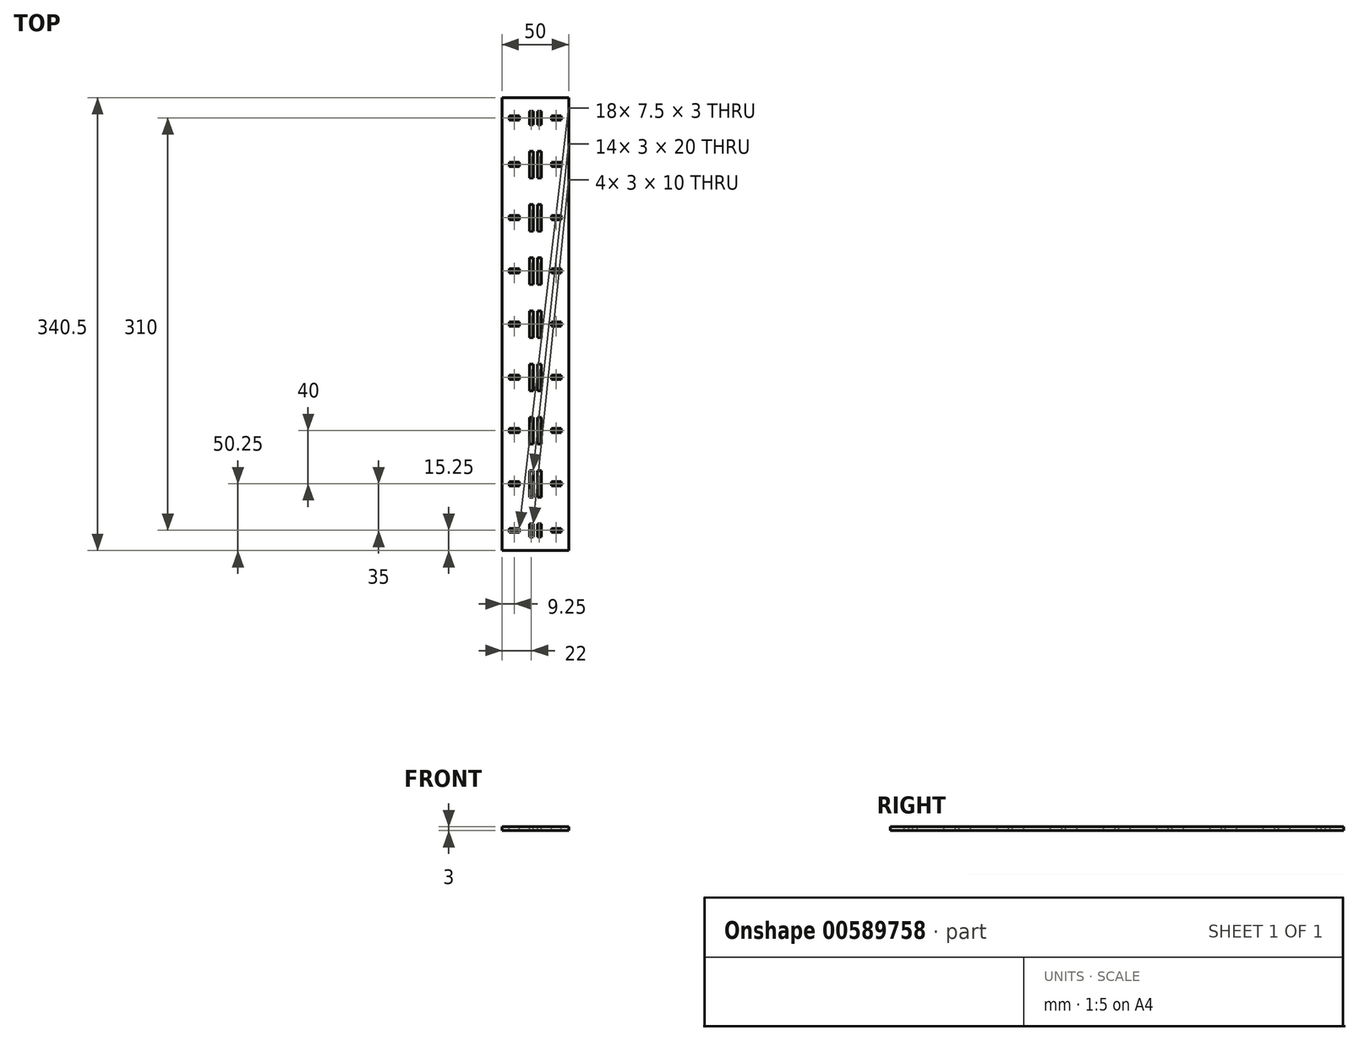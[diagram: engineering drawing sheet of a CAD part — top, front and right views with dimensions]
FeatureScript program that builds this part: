
annotation { "Feature Type Name" : "Feature", "Feature Type Description" : "" }
export const myFeature = defineFeature(function(context is Context, id is Id, definition is map)
    precondition{}
    {
        {
            var Q0;
            Q0=qCreatedBy(makeId("Top.planeOp"),FACE);
            var sketch = newSketch(context, id + "F0", { "sketchPlane" : qUnion([Q0])});
            skLineSegment(sketch, "E0.bottom", {"start": v(25, 140) * mm, "end": v(-25, 140) * mm});
            skLineSegment(sketch, "E0.top", {"start": v(25, -140) * mm, "end": v(-25, -140) * mm});
            skLineSegment(sketch, "E0.left", {"start": v(25, 140) * mm, "end": v(25, -140) * mm});
            skLineSegment(sketch, "E0.right", {"start": v(-25, 140) * mm, "end": v(-25, -140) * mm});
            skPoint(sketch, "E0.middle", {"position": v(0, 0) * mm});
            skSolve(sketch);
        }
        {
            var Q0;
            Q0=makeQuery(id+"F0.imprint","IMPRINT",FACE,{"disambiguationData":[TD([[makeQuery(id+"F0.imprint","IMPRINT",EDGE,{"derivedFrom":sQuery(id+"F0.wireOp",EDGE,"E0.bottom")}),1.0]])]});
            extrude(context, id + "F1", {"entities" : qUnion([Q0]), "depth" : 3 * mm, "offsetDistance" : 25 * mm});
        }
        {
            var Q0;
            Q0=makeQuery(id+"F1.opExtrude","CAP_FACE",FACE,{"disambiguationData":[OSD([sQuery(id+"F0.wireOp",EDGE,"E0.bottom"),sQuery(id+"F0.wireOp",EDGE,"E0.top"),sQuery(id+"F0.wireOp",EDGE,"E0.left"),sQuery(id+"F0.wireOp",EDGE,"E0.right")])],"isStart":false});
            var sketch = newSketch(context, id + "F2", { "sketchPlane" : qUnion([Q0])});
            skLineSegment(sketch, "E1", {"start": v(0, 140) * mm, "end": v(0, -140) * mm, "construction": true});
            skLineSegment(sketch, "E2.bottom", {"start": v(1.5, 140) * mm, "end": v(-1.5, 140) * mm, "construction": true});
            skLineSegment(sketch, "E2.top", {"start": v(1.5, -140) * mm, "end": v(-1.5, -140) * mm, "construction": true});
            skLineSegment(sketch, "E2.left", {"start": v(1.5, 140) * mm, "end": v(1.5, 130) * mm, "construction": true});
            skLineSegment(sketch, "E2.right", {"start": v(-1.5, 140) * mm, "end": v(-1.5, 130) * mm, "construction": true});
            skPoint(sketch, "E2.middle", {"position": v(0, 0) * mm});
            skLineSegment(sketch, "E3.bottom", {"start": v(1.5, 130) * mm, "end": v(4.5, 130) * mm});
            skLineSegment(sketch, "E3.top", {"start": v(1.5, 110) * mm, "end": v(4.5, 110) * mm});
            skLineSegment(sketch, "E3.right", {"start": v(4.5, 130) * mm, "end": v(4.5, 110) * mm});
            skLineSegment(sketch, "E4.trimOffspring", {"start": v(1.5, 110) * mm, "end": v(1.5, -140) * mm, "construction": true});
            skLineSegment(sketch, "E5", {"start": v(1.5, 130) * mm, "end": v(1.5, 110) * mm});
            skLineSegment(sketch, "E6.0.1.0", {"start": v(4.5, 90) * mm, "end": v(4.5, 70) * mm});
            skLineSegment(sketch, "E6.0.1.1", {"start": v(1.5, 90) * mm, "end": v(4.5, 90) * mm});
            skLineSegment(sketch, "E6.0.1.2", {"start": v(1.5, 90) * mm, "end": v(1.5, 70) * mm});
            skLineSegment(sketch, "E6.0.1.3", {"start": v(1.5, 70) * mm, "end": v(4.5, 70) * mm});
            skLineSegment(sketch, "E6.0.2.0", {"start": v(4.5, 50) * mm, "end": v(4.5, 30) * mm});
            skLineSegment(sketch, "E6.0.2.1", {"start": v(1.5, 50) * mm, "end": v(4.5, 50) * mm});
            skLineSegment(sketch, "E6.0.2.2", {"start": v(1.5, 50) * mm, "end": v(1.5, 30) * mm});
            skLineSegment(sketch, "E6.0.2.3", {"start": v(1.5, 30) * mm, "end": v(4.5, 30) * mm});
            skLineSegment(sketch, "E6.0.3.0", {"start": v(4.5, 10) * mm, "end": v(4.5, -10) * mm});
            skLineSegment(sketch, "E6.0.3.1", {"start": v(1.5, 10) * mm, "end": v(4.5, 10) * mm});
            skLineSegment(sketch, "E6.0.3.2", {"start": v(1.5, 10) * mm, "end": v(1.5, -10) * mm});
            skLineSegment(sketch, "E6.0.3.3", {"start": v(1.5, -10) * mm, "end": v(4.5, -10) * mm});
            skLineSegment(sketch, "E6.0.4.0", {"start": v(4.5, -30) * mm, "end": v(4.5, -50) * mm});
            skLineSegment(sketch, "E6.0.4.1", {"start": v(1.5, -30) * mm, "end": v(4.5, -30) * mm});
            skLineSegment(sketch, "E6.0.4.2", {"start": v(1.5, -30) * mm, "end": v(1.5, -50) * mm});
            skLineSegment(sketch, "E6.0.4.3", {"start": v(1.5, -50) * mm, "end": v(4.5, -50) * mm});
            skLineSegment(sketch, "E6.0.5.0", {"start": v(4.5, -70) * mm, "end": v(4.5, -90) * mm});
            skLineSegment(sketch, "E6.0.5.1", {"start": v(1.5, -70) * mm, "end": v(4.5, -70) * mm});
            skLineSegment(sketch, "E6.0.5.2", {"start": v(1.5, -70) * mm, "end": v(1.5, -90) * mm});
            skLineSegment(sketch, "E6.0.5.3", {"start": v(1.5, -90) * mm, "end": v(4.5, -90) * mm});
            skLineSegment(sketch, "E6.0.6.0", {"start": v(4.5, -110) * mm, "end": v(4.5, -130) * mm});
            skLineSegment(sketch, "E6.0.6.1", {"start": v(1.5, -110) * mm, "end": v(4.5, -110) * mm});
            skLineSegment(sketch, "E6.0.6.2", {"start": v(1.5, -110) * mm, "end": v(1.5, -130) * mm});
            skLineSegment(sketch, "E6.0.6.3", {"start": v(1.5, -130) * mm, "end": v(4.5, -130) * mm});
            skLineSegment(sketch, "E6.direction1", {"start": v(4.5, 110) * mm, "end": v(29.5, 110) * mm, "construction": true});
            skLineSegment(sketch, "E6.direction2", {"start": v(4.5, 110) * mm, "end": v(4.5, 70) * mm, "construction": true});
            skLineSegment(sketch, "E7.bottom", {"start": v(-1.5, 130) * mm, "end": v(-4.5, 130) * mm});
            skLineSegment(sketch, "E7.top", {"start": v(-1.5, 110) * mm, "end": v(-4.5, 110) * mm});
            skLineSegment(sketch, "E7.right", {"start": v(-4.5, 130) * mm, "end": v(-4.5, 110) * mm});
            skLineSegment(sketch, "E8.trimOffspring", {"start": v(-1.5, 110) * mm, "end": v(-1.5, -140) * mm, "construction": true});
            skLineSegment(sketch, "E9", {"start": v(-1.5, 130) * mm, "end": v(-1.5, 110) * mm});
            skLineSegment(sketch, "E10.0.1.0", {"start": v(-1.5, 90) * mm, "end": v(-4.5, 90) * mm});
            skLineSegment(sketch, "E10.0.1.1", {"start": v(-1.5, 90) * mm, "end": v(-1.5, 70) * mm});
            skLineSegment(sketch, "E10.0.1.2", {"start": v(-4.5, 90) * mm, "end": v(-4.5, 70) * mm});
            skLineSegment(sketch, "E10.0.1.3", {"start": v(-1.5, 70) * mm, "end": v(-4.5, 70) * mm});
            skLineSegment(sketch, "E10.0.2.0", {"start": v(-1.5, 50) * mm, "end": v(-4.5, 50) * mm});
            skLineSegment(sketch, "E10.0.2.1", {"start": v(-1.5, 50) * mm, "end": v(-1.5, 30) * mm});
            skLineSegment(sketch, "E10.0.2.2", {"start": v(-4.5, 50) * mm, "end": v(-4.5, 30) * mm});
            skLineSegment(sketch, "E10.0.2.3", {"start": v(-1.5, 30) * mm, "end": v(-4.5, 30) * mm});
            skLineSegment(sketch, "E10.0.3.0", {"start": v(-1.5, 10) * mm, "end": v(-4.5, 10) * mm});
            skLineSegment(sketch, "E10.0.3.1", {"start": v(-1.5, 10) * mm, "end": v(-1.5, -10) * mm});
            skLineSegment(sketch, "E10.0.3.2", {"start": v(-4.5, 10) * mm, "end": v(-4.5, -10) * mm});
            skLineSegment(sketch, "E10.0.3.3", {"start": v(-1.5, -10) * mm, "end": v(-4.5, -10) * mm});
            skLineSegment(sketch, "E10.0.4.0", {"start": v(-1.5, -30) * mm, "end": v(-4.5, -30) * mm});
            skLineSegment(sketch, "E10.0.4.1", {"start": v(-1.5, -30) * mm, "end": v(-1.5, -50) * mm});
            skLineSegment(sketch, "E10.0.4.2", {"start": v(-4.5, -30) * mm, "end": v(-4.5, -50) * mm});
            skLineSegment(sketch, "E10.0.4.3", {"start": v(-1.5, -50) * mm, "end": v(-4.5, -50) * mm});
            skLineSegment(sketch, "E10.0.5.0", {"start": v(-1.5, -70) * mm, "end": v(-4.5, -70) * mm});
            skLineSegment(sketch, "E10.0.5.1", {"start": v(-1.5, -70) * mm, "end": v(-1.5, -90) * mm});
            skLineSegment(sketch, "E10.0.5.2", {"start": v(-4.5, -70) * mm, "end": v(-4.5, -90) * mm});
            skLineSegment(sketch, "E10.0.5.3", {"start": v(-1.5, -90) * mm, "end": v(-4.5, -90) * mm});
            skLineSegment(sketch, "E10.0.6.0", {"start": v(-1.5, -110) * mm, "end": v(-4.5, -110) * mm});
            skLineSegment(sketch, "E10.0.6.1", {"start": v(-1.5, -110) * mm, "end": v(-1.5, -130) * mm});
            skLineSegment(sketch, "E10.0.6.2", {"start": v(-4.5, -110) * mm, "end": v(-4.5, -130) * mm});
            skLineSegment(sketch, "E10.0.6.3", {"start": v(-1.5, -130) * mm, "end": v(-4.5, -130) * mm});
            skLineSegment(sketch, "E10.direction1", {"start": v(-4.5, 130) * mm, "end": v(20.5, 130) * mm, "construction": true});
            skLineSegment(sketch, "E10.direction2", {"start": v(-4.5, 130) * mm, "end": v(-4.5, 90) * mm, "construction": true});
            skSolve(sketch);
        }
        {
            var Q0;
            Q0=qSketchRegion(id+"F2",true);
            extrude(context, id + "F3", {"entities" : qUnion([Q0]), "operationType" : NewBodyOperationType.REMOVE, "oppositeDirection" : true, "depth" : 25 * mm, "offsetDistance" : 25 * mm});
        }
        {
            var Q0;
            Q0=makeQuery(id+"F1.opExtrude","CAP_FACE",FACE,{"disambiguationData":[OSD([sQuery(id+"F0.wireOp",EDGE,"E0.bottom"),sQuery(id+"F0.wireOp",EDGE,"E0.top"),sQuery(id+"F0.wireOp",EDGE,"E0.left"),sQuery(id+"F0.wireOp",EDGE,"E0.right")])],"isStart":false});
            var sketch = newSketch(context, id + "F4", { "sketchPlane" : qUnion([Q0])});
            skLineSegment(sketch, "E11", {"start": v(4.5, 120) * mm, "end": v(12, 120) * mm, "construction": true});
            skLineSegment(sketch, "E12", {"start": v(12, 120) * mm, "end": v(19.5, 120) * mm, "construction": true});
            skLineSegment(sketch, "E13.bottom", {"start": v(19.5, 121.5) * mm, "end": v(12, 121.5) * mm});
            skLineSegment(sketch, "E13.top", {"start": v(19.5, 118.5) * mm, "end": v(12, 118.5) * mm});
            skLineSegment(sketch, "E13.left", {"start": v(19.5, 121.5) * mm, "end": v(19.5, 118.5) * mm});
            skLineSegment(sketch, "E13.right", {"start": v(12, 121.5) * mm, "end": v(12, 118.5) * mm});
            skPoint(sketch, "E13.middle", {"position": v(15.75, 120) * mm});
            skLineSegment(sketch, "E14.0.1.0", {"start": v(19.5, 81.5) * mm, "end": v(12, 81.5) * mm});
            skLineSegment(sketch, "E14.0.1.1", {"start": v(12, 81.5) * mm, "end": v(12, 78.5) * mm});
            skLineSegment(sketch, "E14.0.1.2", {"start": v(19.5, 78.5) * mm, "end": v(12, 78.5) * mm});
            skLineSegment(sketch, "E14.0.1.3", {"start": v(19.5, 81.5) * mm, "end": v(19.5, 78.5) * mm});
            skLineSegment(sketch, "E14.0.2.0", {"start": v(19.5, 41.5) * mm, "end": v(12, 41.5) * mm});
            skLineSegment(sketch, "E14.0.2.1", {"start": v(12, 41.5) * mm, "end": v(12, 38.5) * mm});
            skLineSegment(sketch, "E14.0.2.2", {"start": v(19.5, 38.5) * mm, "end": v(12, 38.5) * mm});
            skLineSegment(sketch, "E14.0.2.3", {"start": v(19.5, 41.5) * mm, "end": v(19.5, 38.5) * mm});
            skLineSegment(sketch, "E14.0.3.0", {"start": v(19.5, 1.5) * mm, "end": v(12, 1.5) * mm});
            skLineSegment(sketch, "E14.0.3.1", {"start": v(12, 1.5) * mm, "end": v(12, -1.5) * mm});
            skLineSegment(sketch, "E14.0.3.2", {"start": v(19.5, -1.5) * mm, "end": v(12, -1.5) * mm});
            skLineSegment(sketch, "E14.0.3.3", {"start": v(19.5, 1.5) * mm, "end": v(19.5, -1.5) * mm});
            skLineSegment(sketch, "E14.0.4.0", {"start": v(19.5, -38.5) * mm, "end": v(12, -38.5) * mm});
            skLineSegment(sketch, "E14.0.4.1", {"start": v(12, -38.5) * mm, "end": v(12, -41.5) * mm});
            skLineSegment(sketch, "E14.0.4.2", {"start": v(19.5, -41.5) * mm, "end": v(12, -41.5) * mm});
            skLineSegment(sketch, "E14.0.4.3", {"start": v(19.5, -38.5) * mm, "end": v(19.5, -41.5) * mm});
            skLineSegment(sketch, "E14.0.5.0", {"start": v(19.5, -78.5) * mm, "end": v(12, -78.5) * mm});
            skLineSegment(sketch, "E14.0.5.1", {"start": v(12, -78.5) * mm, "end": v(12, -81.5) * mm});
            skLineSegment(sketch, "E14.0.5.2", {"start": v(19.5, -81.5) * mm, "end": v(12, -81.5) * mm});
            skLineSegment(sketch, "E14.0.5.3", {"start": v(19.5, -78.5) * mm, "end": v(19.5, -81.5) * mm});
            skLineSegment(sketch, "E14.0.6.0", {"start": v(19.5, -118.5) * mm, "end": v(12, -118.5) * mm});
            skLineSegment(sketch, "E14.0.6.1", {"start": v(12, -118.5) * mm, "end": v(12, -121.5) * mm});
            skLineSegment(sketch, "E14.0.6.2", {"start": v(19.5, -121.5) * mm, "end": v(12, -121.5) * mm});
            skLineSegment(sketch, "E14.0.6.3", {"start": v(19.5, -118.5) * mm, "end": v(19.5, -121.5) * mm});
            skLineSegment(sketch, "E14.direction1", {"start": v(12, 118.5) * mm, "end": v(37, 118.5) * mm, "construction": true});
            skLineSegment(sketch, "E14.direction2", {"start": v(12, 118.5) * mm, "end": v(12, 78.5) * mm, "construction": true});
            skLineSegment(sketch, "E15", {"start": v(0, 140) * mm, "end": v(0, 132.73) * mm, "construction": true});
            skPoint(sketch, "E15.endSnap0", {"position": v(0, 140) * mm});
            skLineSegment(sketch, "E16.MirrorCS", {"start": v(-19.5, 121.5) * mm, "end": v(-12, 121.5) * mm});
            skLineSegment(sketch, "E17.MirrorCS", {"start": v(-19.5, 118.5) * mm, "end": v(-12, 118.5) * mm});
            skLineSegment(sketch, "E18.MirrorCS", {"start": v(-12, 121.5) * mm, "end": v(-12, 118.5) * mm});
            skLineSegment(sketch, "E19.MirrorCS", {"start": v(-12, 120) * mm, "end": v(-19.5, 120) * mm, "construction": true});
            skLineSegment(sketch, "E20.MirrorCS", {"start": v(-19.5, 121.5) * mm, "end": v(-19.5, 118.5) * mm});
            skLineSegment(sketch, "E21.MirrorCS", {"start": v(-19.5, -78.5) * mm, "end": v(-19.5, -81.5) * mm});
            skLineSegment(sketch, "E22.MirrorCS", {"start": v(-19.5, 41.5) * mm, "end": v(-19.5, 38.5) * mm});
            skLineSegment(sketch, "E23.MirrorCS", {"start": v(-19.5, 81.5) * mm, "end": v(-12, 81.5) * mm});
            skLineSegment(sketch, "E24.MirrorCS", {"start": v(-12, 81.5) * mm, "end": v(-12, 78.5) * mm});
            skLineSegment(sketch, "E25.MirrorCS", {"start": v(-19.5, 78.5) * mm, "end": v(-12, 78.5) * mm});
            skLineSegment(sketch, "E26.MirrorCS", {"start": v(-19.5, -78.5) * mm, "end": v(-12, -78.5) * mm});
            skLineSegment(sketch, "E27.MirrorCS", {"start": v(-19.5, -38.5) * mm, "end": v(-12, -38.5) * mm});
            skLineSegment(sketch, "E28.MirrorCS", {"start": v(-19.5, -118.5) * mm, "end": v(-12, -118.5) * mm});
            skLineSegment(sketch, "E29.MirrorCS", {"start": v(-12, -38.5) * mm, "end": v(-12, -41.5) * mm});
            skLineSegment(sketch, "E30.MirrorCS", {"start": v(-19.5, -1.5) * mm, "end": v(-12, -1.5) * mm});
            skLineSegment(sketch, "E31.MirrorCS", {"start": v(-12, -118.5) * mm, "end": v(-12, -121.5) * mm});
            skLineSegment(sketch, "E32.MirrorCS", {"start": v(-19.5, -118.5) * mm, "end": v(-19.5, -121.5) * mm});
            skLineSegment(sketch, "E33.MirrorCS", {"start": v(-19.5, -41.5) * mm, "end": v(-12, -41.5) * mm});
            skLineSegment(sketch, "E34.MirrorCS", {"start": v(-19.5, 1.5) * mm, "end": v(-12, 1.5) * mm});
            skLineSegment(sketch, "E35.MirrorCS", {"start": v(-12, 1.5) * mm, "end": v(-12, -1.5) * mm});
            skLineSegment(sketch, "E36.MirrorCS", {"start": v(-12, -78.5) * mm, "end": v(-12, -81.5) * mm});
            skLineSegment(sketch, "E37.MirrorCS", {"start": v(-19.5, 81.5) * mm, "end": v(-19.5, 78.5) * mm});
            skLineSegment(sketch, "E38.MirrorCS", {"start": v(-19.5, 41.5) * mm, "end": v(-12, 41.5) * mm});
            skLineSegment(sketch, "E39.MirrorCS", {"start": v(-19.5, -121.5) * mm, "end": v(-12, -121.5) * mm});
            skLineSegment(sketch, "E40.MirrorCS", {"start": v(-12, 41.5) * mm, "end": v(-12, 38.5) * mm});
            skLineSegment(sketch, "E41.MirrorCS", {"start": v(-19.5, 38.5) * mm, "end": v(-12, 38.5) * mm});
            skLineSegment(sketch, "E42.MirrorCS", {"start": v(-19.5, -81.5) * mm, "end": v(-12, -81.5) * mm});
            skLineSegment(sketch, "E43.MirrorCS", {"start": v(-19.5, 1.5) * mm, "end": v(-19.5, -1.5) * mm});
            skLineSegment(sketch, "E44.MirrorCS", {"start": v(-19.5, -38.5) * mm, "end": v(-19.5, -41.5) * mm});
            skPoint(sketch, "E45.MirrorP", {"position": v(-15.75, 120) * mm});
            skLineSegment(sketch, "E46.MirrorCS", {"start": v(-12, 118.5) * mm, "end": v(-12, 78.5) * mm, "construction": true});
            skLineSegment(sketch, "E47.MirrorCS", {"start": v(-12, 118.5) * mm, "end": v(-37, 118.5) * mm, "construction": true});
            skSolve(sketch);
        }
        {
            var Q0;
            Q0=qSketchRegion(id+"F4",true);
            extrude(context, id + "F5", {"entities" : qUnion([Q0]), "operationType" : NewBodyOperationType.REMOVE, "oppositeDirection" : true, "depth" : 25 * mm, "offsetDistance" : 25 * mm});
        }
        {
            var Q0;
            Q0=makeQuery(id+"F1.opExtrude","CAP_FACE",FACE,{"disambiguationData":[OSD([sQuery(id+"F0.wireOp",EDGE,"E0.bottom"),sQuery(id+"F0.wireOp",EDGE,"E0.top"),sQuery(id+"F0.wireOp",EDGE,"E0.left"),sQuery(id+"F0.wireOp",EDGE,"E0.right")])],"isStart":false});
            var sketch = newSketch(context, id + "F6", { "sketchPlane" : qUnion([Q0])});
            skLineSegment(sketch, "E48.bottom", {"start": v(-25, 140) * mm, "end": v(25, 140) * mm});
            skLineSegment(sketch, "E48.top", {"start": v(-25, 170.25) * mm, "end": v(25, 170.25) * mm});
            skLineSegment(sketch, "E48.left", {"start": v(-25, 140) * mm, "end": v(-25, 170.25) * mm});
            skLineSegment(sketch, "E48.right", {"start": v(25, 140) * mm, "end": v(25, 170.25) * mm});
            skLineSegment(sketch, "E49.MirrorCS", {"start": v(-25, -140) * mm, "end": v(-25, -170.25) * mm});
            skLineSegment(sketch, "E50.MirrorCS", {"start": v(-25, -170.25) * mm, "end": v(25, -170.25) * mm});
            skLineSegment(sketch, "E51.MirrorCS", {"start": v(-25, -140) * mm, "end": v(25, -140) * mm});
            skLineSegment(sketch, "E52.MirrorCS", {"start": v(25, -140) * mm, "end": v(25, -170.25) * mm});
            skSolve(sketch);
        }
        {
            var Q0;
            Q0 = qSketchRegion(id + "F6", true);
            extrude(context, id + "F7", {"entities" : qUnion([Q0]), "operationType" : NewBodyOperationType.ADD, "oppositeDirection" : true, "depth" : 3 * mm, "offsetDistance" : 25 * mm});
        }
        {
            var Q0;
            Q0=makeQuery(id+"F7.boolean.opBoolean","MERGE",FACE,{"derivedFrom":[makeQuery(id+"F1.opExtrude","CAP_FACE",FACE,{"disambiguationData":[OSD([sQuery(id+"F0.wireOp",EDGE,"E0.bottom"),sQuery(id+"F0.wireOp",EDGE,"E0.top"),sQuery(id+"F0.wireOp",EDGE,"E0.left"),sQuery(id+"F0.wireOp",EDGE,"E0.right")])],"isStart":false}),makeQuery(id+"F7.opExtrude","CAP_FACE",FACE,{"disambiguationData":[OSD([sQuery(id+"F6.wireOp",EDGE,"E48.bottom"),sQuery(id+"F6.wireOp",EDGE,"E48.top"),sQuery(id+"F6.wireOp",EDGE,"E48.left"),sQuery(id+"F6.wireOp",EDGE,"E48.right")])],"isStart":true}),makeQuery(id+"F7.opExtrude","CAP_FACE",FACE,{"disambiguationData":[OSD([sQuery(id+"F6.wireOp",EDGE,"E49.MirrorCS"),sQuery(id+"F6.wireOp",EDGE,"E50.MirrorCS"),sQuery(id+"F6.wireOp",EDGE,"E51.MirrorCS"),sQuery(id+"F6.wireOp",EDGE,"E52.MirrorCS")])],"isStart":true})]});
            var sketch = newSketch(context, id + "F8", { "sketchPlane" : qUnion([Q0])});
            skLineSegment(sketch, "E53", {"start": v(-1.5, 130) * mm, "end": v(-1.5, 150) * mm, "construction": true});
            skLineSegment(sketch, "E54.bottom", {"start": v(-1.5, 150) * mm, "end": v(-4.5, 150) * mm});
            skLineSegment(sketch, "E54.top", {"start": v(-1.5, 160) * mm, "end": v(-4.5, 160) * mm});
            skLineSegment(sketch, "E54.left", {"start": v(-1.5, 150) * mm, "end": v(-1.5, 160) * mm});
            skLineSegment(sketch, "E54.right", {"start": v(-4.5, 150) * mm, "end": v(-4.5, 160) * mm});
            skLineSegment(sketch, "E55.MirrorCS", {"start": v(4.5, 150) * mm, "end": v(4.5, 160) * mm});
            skLineSegment(sketch, "E56.MirrorCS", {"start": v(1.5, 150) * mm, "end": v(1.5, 160) * mm});
            skLineSegment(sketch, "E57.MirrorCS", {"start": v(1.5, 160) * mm, "end": v(4.5, 160) * mm});
            skLineSegment(sketch, "E58.MirrorCS", {"start": v(1.5, 150) * mm, "end": v(4.5, 150) * mm});
            skLineSegment(sketch, "E59.MirrorCS", {"start": v(1.5, -150) * mm, "end": v(4.5, -150) * mm});
            skLineSegment(sketch, "E60.MirrorCS", {"start": v(-1.5, -150) * mm, "end": v(-4.5, -150) * mm});
            skLineSegment(sketch, "E61.MirrorCS", {"start": v(1.5, -160) * mm, "end": v(4.5, -160) * mm});
            skLineSegment(sketch, "E62.MirrorCS", {"start": v(-1.5, -160) * mm, "end": v(-4.5, -160) * mm});
            skLineSegment(sketch, "E63.MirrorCS", {"start": v(1.5, -150) * mm, "end": v(1.5, -160) * mm});
            skLineSegment(sketch, "E64.MirrorCS", {"start": v(4.5, -150) * mm, "end": v(4.5, -160) * mm});
            skLineSegment(sketch, "E65.MirrorCS", {"start": v(-1.5, -150) * mm, "end": v(-1.5, -160) * mm});
            skLineSegment(sketch, "E66.MirrorCS", {"start": v(-4.5, -150) * mm, "end": v(-4.5, -160) * mm});
            skSolve(sketch);
        }
        {
            var Q0;
            Q0 = qSketchRegion(id + "F8", true);
            extrude(context, id + "F9", {"entities" : qUnion([Q0]), "operationType" : NewBodyOperationType.REMOVE, "oppositeDirection" : true, "depth" : 25 * mm, "offsetDistance" : 25 * mm});
        }
        {
            var Q0;
            Q0=makeQuery(id+"F7.boolean.opBoolean","MERGE",FACE,{"derivedFrom":[makeQuery(id+"F1.opExtrude","CAP_FACE",FACE,{"disambiguationData":[OSD([sQuery(id+"F0.wireOp",EDGE,"E0.bottom"),sQuery(id+"F0.wireOp",EDGE,"E0.top"),sQuery(id+"F0.wireOp",EDGE,"E0.left"),sQuery(id+"F0.wireOp",EDGE,"E0.right")])],"isStart":false}),makeQuery(id+"F7.opExtrude","CAP_FACE",FACE,{"disambiguationData":[OSD([sQuery(id+"F6.wireOp",EDGE,"E48.bottom"),sQuery(id+"F6.wireOp",EDGE,"E48.top"),sQuery(id+"F6.wireOp",EDGE,"E48.left"),sQuery(id+"F6.wireOp",EDGE,"E48.right")])],"isStart":true}),makeQuery(id+"F7.opExtrude","CAP_FACE",FACE,{"disambiguationData":[OSD([sQuery(id+"F6.wireOp",EDGE,"E49.MirrorCS"),sQuery(id+"F6.wireOp",EDGE,"E50.MirrorCS"),sQuery(id+"F6.wireOp",EDGE,"E51.MirrorCS"),sQuery(id+"F6.wireOp",EDGE,"E52.MirrorCS")])],"isStart":true})]});
            var sketch = newSketch(context, id + "F10", { "sketchPlane" : qUnion([Q0])});
            skLineSegment(sketch, "E67", {"start": v(-4.5, -155) * mm, "end": v(-12, -155) * mm, "construction": true});
            skLineSegment(sketch, "E68", {"start": v(-12, -155) * mm, "end": v(-19.5, -155) * mm, "construction": true});
            skLineSegment(sketch, "E69.bottom", {"start": v(-12, -153.5) * mm, "end": v(-19.5, -153.5) * mm});
            skLineSegment(sketch, "E69.top", {"start": v(-12, -156.5) * mm, "end": v(-19.5, -156.5) * mm});
            skLineSegment(sketch, "E69.left", {"start": v(-12, -153.5) * mm, "end": v(-12, -156.5) * mm});
            skLineSegment(sketch, "E69.right", {"start": v(-19.5, -153.5) * mm, "end": v(-19.5, -156.5) * mm});
            skPoint(sketch, "E69.middle", {"position": v(-15.75, -155) * mm});
            skLineSegment(sketch, "E70.MirrorCS", {"start": v(12, -153.5) * mm, "end": v(12, -156.5) * mm});
            skLineSegment(sketch, "E71.MirrorCS", {"start": v(12, -156.5) * mm, "end": v(19.5, -156.5) * mm});
            skLineSegment(sketch, "E72.MirrorCS", {"start": v(12, -153.5) * mm, "end": v(19.5, -153.5) * mm});
            skLineSegment(sketch, "E73.MirrorCS", {"start": v(19.5, -153.5) * mm, "end": v(19.5, -156.5) * mm});
            skLineSegment(sketch, "E74.MirrorCS", {"start": v(4.5, -155) * mm, "end": v(12, -155) * mm, "construction": true});
            skLineSegment(sketch, "E75.MirrorCS", {"start": v(12, -155) * mm, "end": v(19.5, -155) * mm, "construction": true});
            skPoint(sketch, "E76.MirrorP", {"position": v(15.75, -155) * mm});
            skLineSegment(sketch, "E77.MirrorCS", {"start": v(-12, 153.5) * mm, "end": v(-12, 156.5) * mm});
            skLineSegment(sketch, "E78.MirrorCS", {"start": v(12, 153.5) * mm, "end": v(12, 156.5) * mm});
            skLineSegment(sketch, "E79.MirrorCS", {"start": v(12, 156.5) * mm, "end": v(19.5, 156.5) * mm});
            skLineSegment(sketch, "E80.MirrorCS", {"start": v(12, 153.5) * mm, "end": v(19.5, 153.5) * mm});
            skLineSegment(sketch, "E81.MirrorCS", {"start": v(19.5, 153.5) * mm, "end": v(19.5, 156.5) * mm});
            skLineSegment(sketch, "E82.MirrorCS", {"start": v(12, 155) * mm, "end": v(19.5, 155) * mm, "construction": true});
            skLineSegment(sketch, "E83.MirrorCS", {"start": v(-12, 153.5) * mm, "end": v(-19.5, 153.5) * mm});
            skLineSegment(sketch, "E84.MirrorCS", {"start": v(-12, 156.5) * mm, "end": v(-19.5, 156.5) * mm});
            skLineSegment(sketch, "E85.MirrorCS", {"start": v(-19.5, 153.5) * mm, "end": v(-19.5, 156.5) * mm});
            skLineSegment(sketch, "E86.MirrorCS", {"start": v(-12, 155) * mm, "end": v(-19.5, 155) * mm, "construction": true});
            skLineSegment(sketch, "E87.MirrorCS", {"start": v(4.5, 155) * mm, "end": v(12, 155) * mm, "construction": true});
            skLineSegment(sketch, "E88.MirrorCS", {"start": v(-4.5, 155) * mm, "end": v(-12, 155) * mm, "construction": true});
            skPoint(sketch, "E89.MirrorP", {"position": v(15.75, 155) * mm});
            skPoint(sketch, "E90.MirrorP", {"position": v(-15.75, 155) * mm});
            skSolve(sketch);
        }
        {
            var Q0;
            Q0 = qSketchRegion(id + "F10", true);
            extrude(context, id + "F11", {"entities" : qUnion([Q0]), "operationType" : NewBodyOperationType.REMOVE, "oppositeDirection" : true, "depth" : 25 * mm, "offsetDistance" : 25 * mm});
        }
    });
